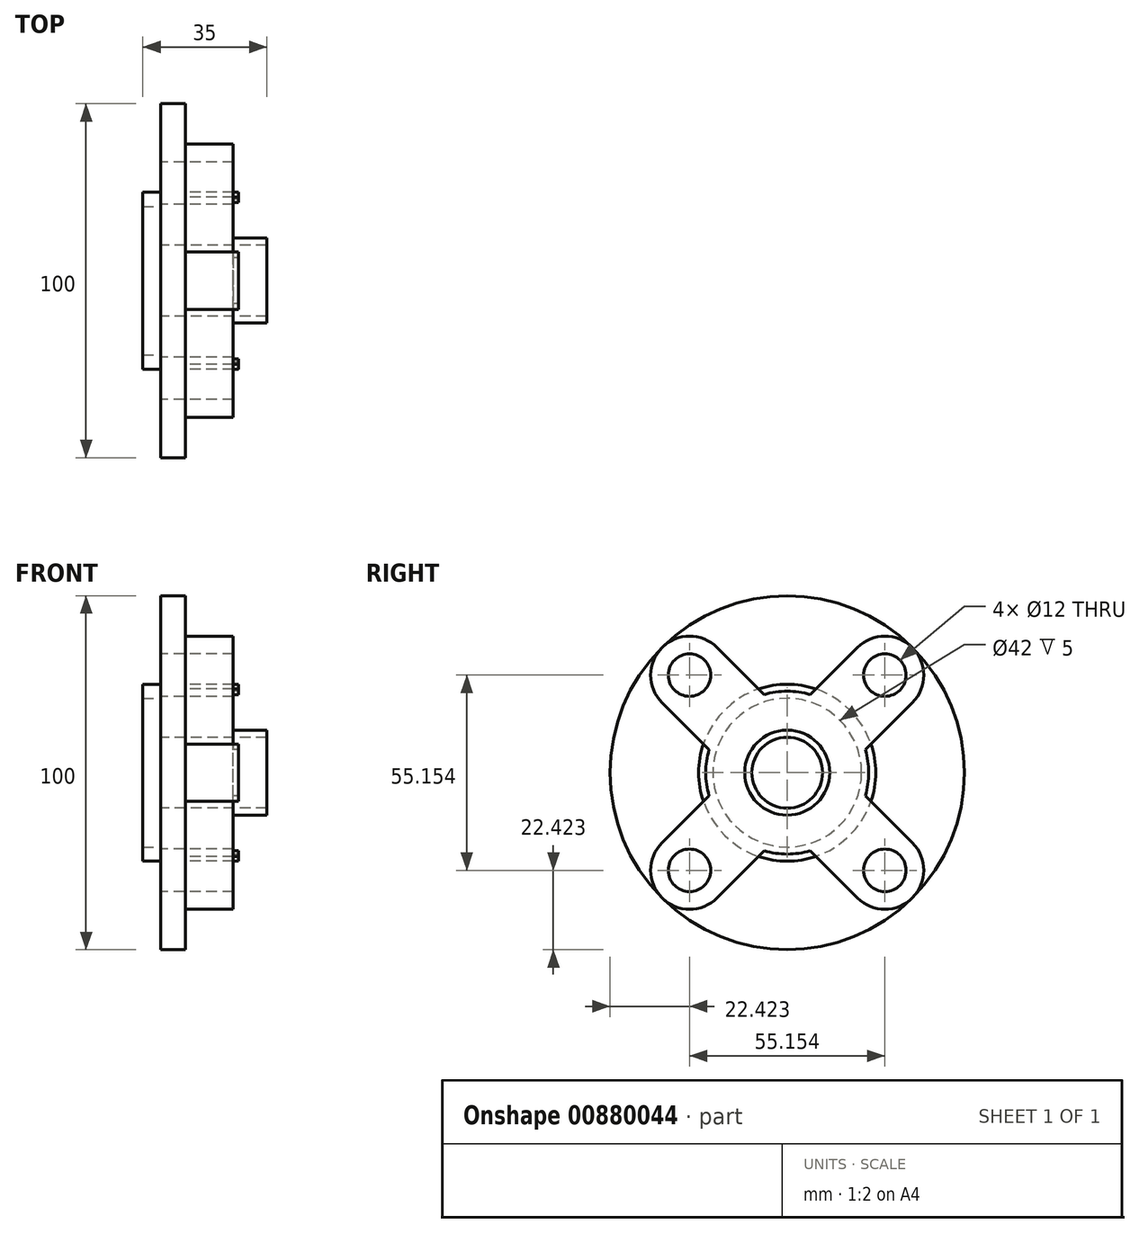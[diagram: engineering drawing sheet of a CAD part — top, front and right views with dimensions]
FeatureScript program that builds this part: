
annotation { "Feature Type Name" : "Feature", "Feature Type Description" : "" }
export const myFeature = defineFeature(function(context is Context, id is Id, definition is map)
    precondition{}
    {
        {
            var Q0;
            Q0=qCreatedBy(makeId("Right.planeOp"),FACE);
            var sketch = newSketch(context, id + "F0", { "sketchPlane" : qUnion([Q0])});
            skArc(sketch, "E0", {"start": v(-23.65, 8.1) * mm, "mid": v(-25, 0) * mm, "end": v(-23.65, -8.1) * mm});
            skCircle(sketch, "E1", {"center": v(0, 0) * mm, "radius": 10 * mm});
            skCircle(sketch, "E2", {"center": v(0, 0) * mm, "radius": 50 * mm});
            skLineSegment(sketch, "E3", {"start": v(0, 0) * mm, "end": v(-53.33, 53.33) * mm, "construction": true});
            skArc(sketch, "E4", {"start": v(-19.8, 35.36) * mm, "mid": v(-35.36, 35.36) * mm, "end": v(-35.36, 19.8) * mm});
            skPoint(sketch, "E4.first.point", {"position": v(-35.36, 35.36) * mm});
            skLineSegment(sketch, "E5", {"start": v(-27.58, 27.58) * mm, "end": v(-35.36, 19.8) * mm, "construction": true});
            skLineSegment(sketch, "E6", {"start": v(-27.58, 27.58) * mm, "end": v(-19.8, 35.36) * mm, "construction": true});
            skLineSegment(sketch, "E7", {"start": v(-35.36, 19.8) * mm, "end": v(-22.06, 6.5) * mm});
            skLineSegment(sketch, "E8", {"start": v(-19.8, 35.36) * mm, "end": v(-6.5, 22.06) * mm});
            skCircle(sketch, "E9", {"center": v(-27.58, 27.58) * mm, "radius": 6 * mm});
            skLineSegment(sketch, "E10.1.0", {"start": v(35.36, 19.8) * mm, "end": v(22.06, 6.5) * mm});
            skLineSegment(sketch, "E10.1.1", {"start": v(27.58, 27.58) * mm, "end": v(35.36, 19.8) * mm, "construction": true});
            skPoint(sketch, "E10.1.2", {"position": v(35.36, 35.36) * mm});
            skArc(sketch, "E10.1.3", {"start": v(35.36, 19.8) * mm, "mid": v(35.36, 35.36) * mm, "end": v(19.8, 35.36) * mm});
            skLineSegment(sketch, "E10.1.4", {"start": v(27.58, 27.58) * mm, "end": v(19.8, 35.36) * mm, "construction": true});
            skLineSegment(sketch, "E10.1.5", {"start": v(19.8, 35.36) * mm, "end": v(6.5, 22.06) * mm});
            skCircle(sketch, "E10.1.6", {"center": v(27.58, 27.58) * mm, "radius": 6 * mm});
            skLineSegment(sketch, "E10.1.7", {"start": v(0, 0) * mm, "end": v(53.33, 53.33) * mm, "construction": true});
            skLineSegment(sketch, "E10.2.0", {"start": v(19.8, -35.36) * mm, "end": v(6.5, -22.06) * mm});
            skLineSegment(sketch, "E10.2.1", {"start": v(27.58, -27.58) * mm, "end": v(19.8, -35.36) * mm, "construction": true});
            skPoint(sketch, "E10.2.2", {"position": v(35.36, -35.36) * mm});
            skArc(sketch, "E10.2.3", {"start": v(19.8, -35.36) * mm, "mid": v(35.36, -35.36) * mm, "end": v(35.36, -19.8) * mm});
            skLineSegment(sketch, "E10.2.4", {"start": v(27.58, -27.58) * mm, "end": v(35.36, -19.8) * mm, "construction": true});
            skLineSegment(sketch, "E10.2.5", {"start": v(35.36, -19.8) * mm, "end": v(22.06, -6.5) * mm});
            skCircle(sketch, "E10.2.6", {"center": v(27.58, -27.58) * mm, "radius": 6 * mm});
            skLineSegment(sketch, "E10.2.7", {"start": v(0, 0) * mm, "end": v(53.33, -53.33) * mm, "construction": true});
            skLineSegment(sketch, "E10.3.0", {"start": v(-35.36, -19.8) * mm, "end": v(-22.06, -6.5) * mm});
            skLineSegment(sketch, "E10.3.1", {"start": v(-27.58, -27.58) * mm, "end": v(-35.36, -19.8) * mm, "construction": true});
            skPoint(sketch, "E10.3.2", {"position": v(-35.36, -35.36) * mm});
            skArc(sketch, "E10.3.3", {"start": v(-35.36, -19.8) * mm, "mid": v(-35.36, -35.36) * mm, "end": v(-19.8, -35.36) * mm});
            skLineSegment(sketch, "E10.3.4", {"start": v(-27.58, -27.58) * mm, "end": v(-19.8, -35.36) * mm, "construction": true});
            skLineSegment(sketch, "E10.3.5", {"start": v(-19.8, -35.36) * mm, "end": v(-6.5, -22.06) * mm});
            skCircle(sketch, "E10.3.6", {"center": v(-27.58, -27.58) * mm, "radius": 6 * mm});
            skLineSegment(sketch, "E10.3.7", {"start": v(0, 0) * mm, "end": v(-53.33, -53.33) * mm, "construction": true});
            skLineSegment(sketch, "E10.anchor1", {"start": v(0, 0) * mm, "end": v(-23.65, 8.1) * mm, "construction": true});
            skLineSegment(sketch, "E10.anchor2", {"start": v(0, 0) * mm, "end": v(-8.1, -23.65) * mm, "construction": true});
            skArc(sketch, "E11.trimOffspring", {"start": v(8.1, 23.65) * mm, "mid": v(0, 25) * mm, "end": v(-8.1, 23.65) * mm});
            skArc(sketch, "E12.trimOffspring", {"start": v(23.65, -8.1) * mm, "mid": v(25, 0) * mm, "end": v(23.65, 8.1) * mm});
            skArc(sketch, "E13.trimOffspring", {"start": v(-8.1, -23.65) * mm, "mid": v(0, -25) * mm, "end": v(8.1, -23.65) * mm});
            skCircle(sketch, "E14.0", {"center": v(0, 0) * mm, "radius": 12 * mm});
            skArc(sketch, "E15.0", {"start": v(6.5, 22.06) * mm, "mid": v(0, 23) * mm, "end": v(-6.5, 22.06) * mm});
            skArc(sketch, "E16.0", {"start": v(22.06, -6.5) * mm, "mid": v(23, 0) * mm, "end": v(22.06, 6.5) * mm});
            skArc(sketch, "E17.0", {"start": v(-6.5, -22.06) * mm, "mid": v(0, -23) * mm, "end": v(6.5, -22.06) * mm});
            skArc(sketch, "E18.0", {"start": v(-22.06, 6.5) * mm, "mid": v(-23, 0) * mm, "end": v(-22.06, -6.5) * mm});
            skCircle(sketch, "E19", {"center": v(0, 0) * mm, "radius": 25 * mm});
            skCircle(sketch, "E20", {"center": v(0, 0) * mm, "radius": 21 * mm});
            skSolve(sketch);
        }
        {
            var Q0;
            Q0=makeQuery(id+"F0.imprint","IMPRINT",FACE,{"disambiguationData":[TD([[makeQuery(id+"F0.imprint","IMPRINT",EDGE,{"derivedFrom":sQuery(id+"F0.wireOp",EDGE,"E1")}),-1.0]])]});
            extrude(context, id + "F1", {"entities" : qUnion([Q0]), "depth" : 30 * mm});
        }
        {
            var Q0;
            Q0=makeQuery(id+"F0.imprint","IMPRINT",FACE,{"disambiguationData":[TD([[makeQuery(id+"F0.imprint","IMPRINT",EDGE,{"derivedFrom":sQuery(id+"F0.wireOp",EDGE,"E14.0")}),-1.0]])]});
            var Q1;
            {var subQ1=sQuery(id+"F0.wireOp",EDGE,"E15.0");Q1=makeQuery(id+"F0.imprint","IMPRINT",FACE,{"disambiguationData":[TD([[makeQuery(id+"F0.imprint","IMPRINT",EDGE,{"derivedFrom":subQ1}),1.0]])]});}
            extrude(context, id + "F2", {"entities" : qUnion([Q0, Q1]), "operationType" : NewBodyOperationType.ADD, "depth" : 20.5 * mm});
        }
        {
            var Q0;
            {var subQ0=sQuery(id+"F0.wireOp",EDGE,"E18.0");Q0=makeQuery(id+"F0.imprint","IMPRINT",FACE,{"disambiguationData":[TD([[makeQuery(id+"F0.imprint","IMPRINT",EDGE,{"derivedFrom":subQ0}),-1.0]])]});}
            var Q1;
            {var subQ0=sQuery(id+"F0.wireOp",EDGE,"E15.0");Q1=makeQuery(id+"F0.imprint","IMPRINT",FACE,{"disambiguationData":[TD([[makeQuery(id+"F0.imprint","IMPRINT",EDGE,{"derivedFrom":subQ0}),-1.0]])]});}
            var Q2;
            {var subQ0=sQuery(id+"F0.wireOp",EDGE,"E16.0");Q2=makeQuery(id+"F0.imprint","IMPRINT",FACE,{"disambiguationData":[TD([[makeQuery(id+"F0.imprint","IMPRINT",EDGE,{"derivedFrom":subQ0}),-1.0]])]});}
            var Q3;
            {var subQ0=sQuery(id+"F0.wireOp",EDGE,"E17.0");Q3=makeQuery(id+"F0.imprint","IMPRINT",FACE,{"disambiguationData":[TD([[makeQuery(id+"F0.imprint","IMPRINT",EDGE,{"derivedFrom":subQ0}),-1.0]])]});}
            extrude(context, id + "F3", {"entities" : qUnion([Q0, Q1, Q2, Q3]), "operationType" : NewBodyOperationType.ADD, "depth" : 22 * mm});
        }
        {
            var Q0;
            Q0=makeQuery(id+"F0.imprint","IMPRINT",FACE,{"disambiguationData":[TD([[makeQuery(id+"F0.imprint","IMPRINT",EDGE,{"derivedFrom":sQuery(id+"F0.wireOp",EDGE,"E9")}),-1.0]])]});
            var Q1;
            Q1=makeQuery(id+"F0.imprint","IMPRINT",FACE,{"disambiguationData":[TD([[makeQuery(id+"F0.imprint","IMPRINT",EDGE,{"derivedFrom":sQuery(id+"F0.wireOp",EDGE,"E10.3.6")}),-1.0]])]});
            var Q2;
            Q2=makeQuery(id+"F0.imprint","IMPRINT",FACE,{"disambiguationData":[TD([[makeQuery(id+"F0.imprint","IMPRINT",EDGE,{"derivedFrom":sQuery(id+"F0.wireOp",EDGE,"E10.2.6")}),-1.0]])]});
            var Q3;
            Q3=makeQuery(id+"F0.imprint","IMPRINT",FACE,{"disambiguationData":[TD([[makeQuery(id+"F0.imprint","IMPRINT",EDGE,{"derivedFrom":sQuery(id+"F0.wireOp",EDGE,"E10.1.6")}),-1.0]])]});
            var Q4;
            Q4=makeQuery(id+"F2.opExtrude","CAP_FACE",FACE,{"disambiguationData":[OSD([sQuery(id+"F0.wireOp",EDGE,"E7"),sQuery(id+"F0.wireOp",EDGE,"E8"),sQuery(id+"F0.wireOp",EDGE,"E10.1.0"),sQuery(id+"F0.wireOp",EDGE,"E10.1.5"),sQuery(id+"F0.wireOp",EDGE,"E10.2.0"),sQuery(id+"F0.wireOp",EDGE,"E10.2.5"),sQuery(id+"F0.wireOp",EDGE,"E10.3.0"),sQuery(id+"F0.wireOp",EDGE,"E10.3.5"),sQuery(id+"F0.wireOp",EDGE,"E14.0"),sQuery(id+"F0.wireOp",EDGE,"E15.0"),sQuery(id+"F0.wireOp",EDGE,"E16.0"),sQuery(id+"F0.wireOp",EDGE,"E17.0"),sQuery(id+"F0.wireOp",EDGE,"E18.0"),sQuery(id+"F0.wireOp",EDGE,"E19")])],"isStart":false});
            extrude(context, id + "F4", {"entities" : qUnion([Q0, Q1, Q2, Q3]), "operationType" : NewBodyOperationType.ADD, "endBound" : BoundingType.UP_TO_SURFACE, "endBoundEntityFace" : qUnion([Q4]), "depth" : 14.14 * mm});
        }
        {
            var Q0;
            {var subQ6=sQuery(id+"F0.wireOp",EDGE,"E4");var subQ9=sQuery(id+"F0.wireOp",EDGE,"E2");var subQ10=makeQuery(id+"F0.imprint","INTERSECT",VERTEX,{"derivedFrom":[subQ9,subQ6]});Q0=makeQuery(id+"F0.imprint","IMPRINT",FACE,{"disambiguationData":[TD([[makeQuery(id+"F0.imprint","IMPRINT",EDGE,{"disambiguationData":[TD([[subQ10,-1.0]])],"derivedFrom":subQ9}),1.0]])]});}
            var Q1;
            {var subQ3=sQuery(id+"F0.wireOp",EDGE,"E2");var subQ6=sQuery(id+"F0.wireOp",EDGE,"E4");var subQ10=makeQuery(id+"F0.imprint","INTERSECT",VERTEX,{"derivedFrom":[subQ3,subQ6]});Q1=makeQuery(id+"F0.imprint","IMPRINT",FACE,{"disambiguationData":[TD([[makeQuery(id+"F0.imprint","IMPRINT",EDGE,{"disambiguationData":[TD([[subQ10,1.0]])],"derivedFrom":subQ3}),1.0]])]});}
            var Q2;
            {var subQ1=sQuery(id+"F0.wireOp",EDGE,"E10.3.3");var subQ3=sQuery(id+"F0.wireOp",EDGE,"E2");var subQ4=makeQuery(id+"F0.imprint","INTERSECT",VERTEX,{"derivedFrom":[subQ3,subQ1]});Q2=makeQuery(id+"F0.imprint","IMPRINT",FACE,{"disambiguationData":[TD([[makeQuery(id+"F0.imprint","IMPRINT",EDGE,{"disambiguationData":[TD([[subQ4,-1.0]])],"derivedFrom":subQ3}),1.0]])]});}
            var Q3;
            {var subQ0=sQuery(id+"F0.wireOp",EDGE,"E10.1.3");var subQ3=sQuery(id+"F0.wireOp",EDGE,"E2");var subQ4=makeQuery(id+"F0.imprint","INTERSECT",VERTEX,{"derivedFrom":[subQ3,subQ0]});Q3=makeQuery(id+"F0.imprint","IMPRINT",FACE,{"disambiguationData":[TD([[makeQuery(id+"F0.imprint","IMPRINT",EDGE,{"disambiguationData":[TD([[subQ4,1.0]])],"derivedFrom":subQ3}),1.0]])]});}
            extrude(context, id + "F5", {"entities" : qUnion([Q0, Q1, Q2, Q3]), "operationType" : NewBodyOperationType.ADD, "depth" : 7 * mm});
        }
        {
            var Q0;
            {var subQ1=sQuery(id+"F0.wireOp",EDGE,"E15.0");Q0=makeQuery(id+"F0.imprint","IMPRINT",FACE,{"disambiguationData":[TD([[makeQuery(id+"F0.imprint","IMPRINT",EDGE,{"derivedFrom":subQ1}),1.0]])]});}
            var Q1;
            {var subQ0=sQuery(id+"F0.wireOp",EDGE,"E18.0");Q1=makeQuery(id+"F0.imprint","IMPRINT",FACE,{"disambiguationData":[TD([[makeQuery(id+"F0.imprint","IMPRINT",EDGE,{"derivedFrom":subQ0}),-1.0]])]});}
            var Q2;
            {var subQ0=sQuery(id+"F0.wireOp",EDGE,"E15.0");Q2=makeQuery(id+"F0.imprint","IMPRINT",FACE,{"disambiguationData":[TD([[makeQuery(id+"F0.imprint","IMPRINT",EDGE,{"derivedFrom":subQ0}),-1.0]])]});}
            var Q3;
            {var subQ0=sQuery(id+"F0.wireOp",EDGE,"E16.0");Q3=makeQuery(id+"F0.imprint","IMPRINT",FACE,{"disambiguationData":[TD([[makeQuery(id+"F0.imprint","IMPRINT",EDGE,{"derivedFrom":subQ0}),-1.0]])]});}
            var Q4;
            {var subQ0=sQuery(id+"F0.wireOp",EDGE,"E17.0");Q4=makeQuery(id+"F0.imprint","IMPRINT",FACE,{"disambiguationData":[TD([[makeQuery(id+"F0.imprint","IMPRINT",EDGE,{"derivedFrom":subQ0}),-1.0]])]});}
            extrude(context, id + "F6", {"entities" : qUnion([Q0, Q1, Q2, Q3, Q4]), "operationType" : NewBodyOperationType.ADD, "oppositeDirection" : true, "depth" : 5 * mm});
        }
    });
